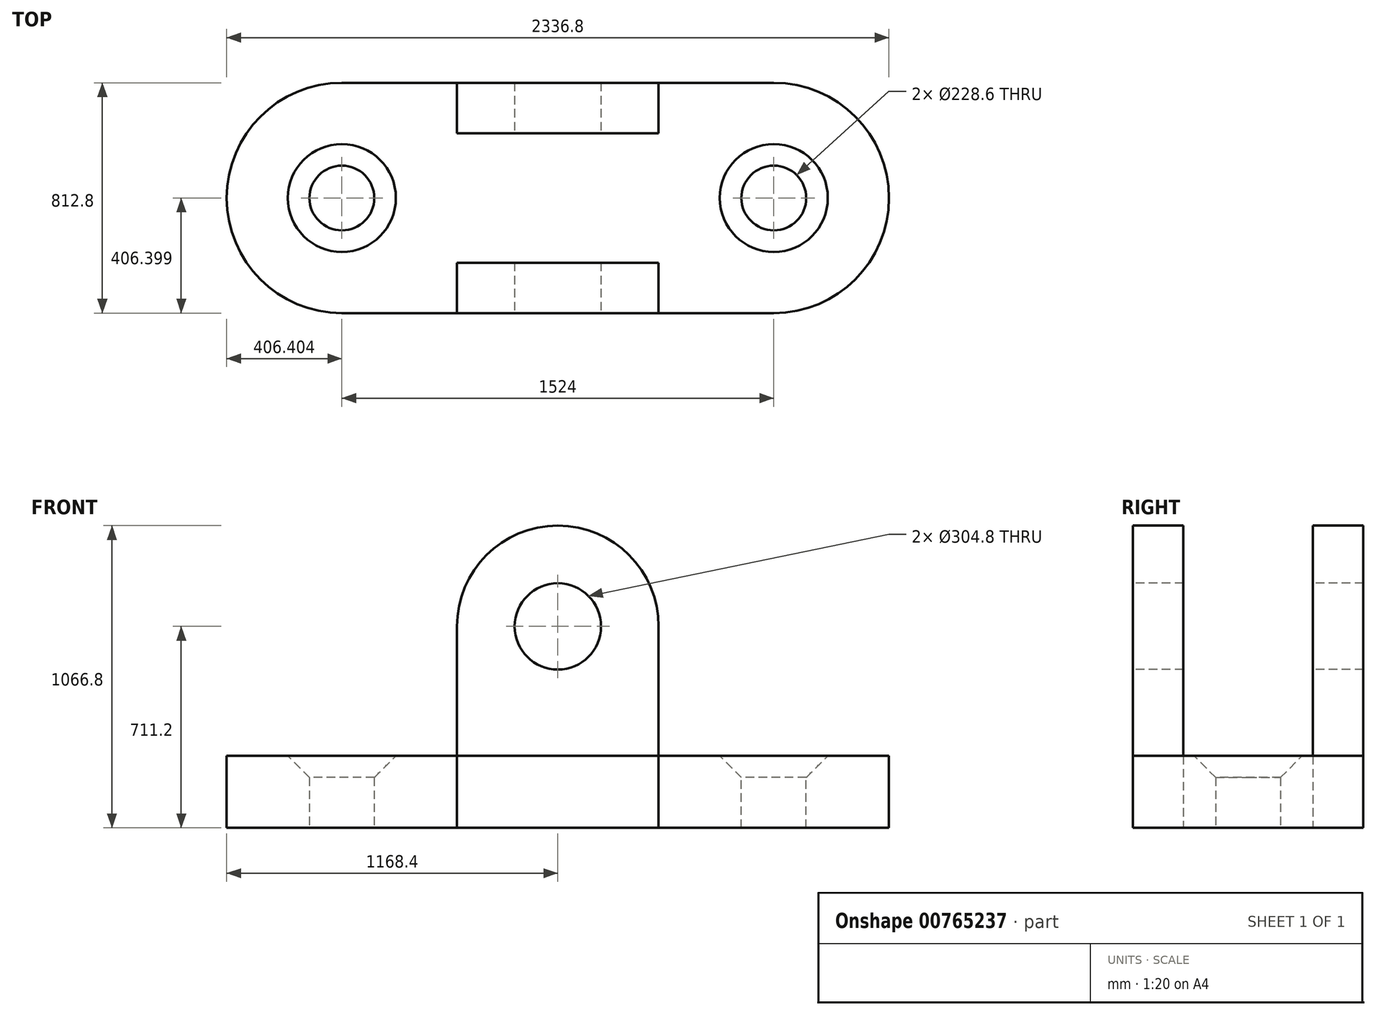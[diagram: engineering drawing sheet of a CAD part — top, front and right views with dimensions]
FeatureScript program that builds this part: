
annotation { "Feature Type Name" : "Feature", "Feature Type Description" : "" }
export const myFeature = defineFeature(function(context is Context, id is Id, definition is map)
    precondition{}
    {
        {
            var Q0;
            Q0=qCreatedBy(makeId("Top.planeOp"),FACE);
            var sketch = newSketch(context, id + "F0", { "sketchPlane" : qUnion([Q0])});
            skLineSegment(sketch, "E0.top", {"start": v(-545.79, -124.18) * mm, "end": v(1791.01, -124.18) * mm});
            skLineSegment(sketch, "E0.left", {"start": v(-545.79, 688.62) * mm, "end": v(-545.79, -124.18) * mm});
            skLineSegment(sketch, "E0.right", {"start": v(1791.01, 688.62) * mm, "end": v(1791.01, -124.18) * mm});
            skLineSegment(sketch, "E1", {"start": v(-545.79, 688.62) * mm, "end": v(1791.01, 688.62) * mm});
            skLineSegment(sketch, "E2", {"start": v(-545.79, 688.62) * mm, "end": v(-545.79, 282.22) * mm});
            skLineSegment(sketch, "E3", {"start": v(-545.79, 282.22) * mm, "end": v(-139.39, 282.22) * mm});
            skCircle(sketch, "E4", {"center": v(-139.39, 282.22) * mm, "radius": 406.4 * mm});
            skLineSegment(sketch, "E5", {"start": v(-139.39, 282.22) * mm, "end": v(-253.69, 282.22) * mm});
            skLineSegment(sketch, "E6", {"start": v(-139.39, 282.22) * mm, "end": v(-342.59, 282.22) * mm});
            skCircle(sketch, "E7", {"center": v(-139.39, 282.22) * mm, "radius": 114.3 * mm});
            skLineSegment(sketch, "E8", {"start": v(1791.01, 688.62) * mm, "end": v(1791.01, 282.22) * mm});
            skLineSegment(sketch, "E9", {"start": v(1791.01, 282.22) * mm, "end": v(1384.61, 282.22) * mm});
            skLineSegment(sketch, "E10", {"start": v(1384.61, 282.22) * mm, "end": v(1498.91, 282.22) * mm});
            skLineSegment(sketch, "E11", {"start": v(1384.61, 282.22) * mm, "end": v(1587.81, 282.22) * mm});
            skCircle(sketch, "E12", {"center": v(1384.61, 282.22) * mm, "radius": 406.4 * mm});
            skLineSegment(sketch, "E13", {"start": v(-139.39, 282.22) * mm, "end": v(267.01, 282.22) * mm});
            skLineSegment(sketch, "E14", {"start": v(267.01, 282.22) * mm, "end": v(267.01, 688.62) * mm});
            skLineSegment(sketch, "E15", {"start": v(267.01, 282.22) * mm, "end": v(267.01, -124.18) * mm});
            skLineSegment(sketch, "E16", {"start": v(1384.61, 282.22) * mm, "end": v(978.21, 282.22) * mm});
            skLineSegment(sketch, "E17", {"start": v(978.21, 282.22) * mm, "end": v(978.21, 688.62) * mm});
            skLineSegment(sketch, "E18", {"start": v(978.21, 282.22) * mm, "end": v(978.21, -124.18) * mm});
            skLineSegment(sketch, "E19", {"start": v(267.01, -124.18) * mm, "end": v(267.01, 53.62) * mm});
            skLineSegment(sketch, "E20", {"start": v(978.21, -124.18) * mm, "end": v(978.21, 53.62) * mm});
            skLineSegment(sketch, "E21", {"start": v(267.01, 53.62) * mm, "end": v(978.21, 53.62) * mm});
            skLineSegment(sketch, "E22", {"start": v(267.01, 688.62) * mm, "end": v(267.01, 510.82) * mm});
            skLineSegment(sketch, "E23", {"start": v(978.21, 688.62) * mm, "end": v(978.21, 510.82) * mm});
            skLineSegment(sketch, "E24", {"start": v(267.01, 510.82) * mm, "end": v(978.21, 510.82) * mm});
            skSolve(sketch);
        }
        {
            var Q0;
            {var subQ5=sQuery(id+"F0.wireOp",EDGE,"E21");Q0=makeQuery(id+"F0.imprint","IMPRINT",FACE,{"disambiguationData":[TD([[makeQuery(id+"F0.imprint","IMPRINT",EDGE,{"derivedFrom":subQ5}),-1.0]])]});}
            var Q1;
            {var subQ5=sQuery(id+"F0.wireOp",EDGE,"E24");Q1=makeQuery(id+"F0.imprint","IMPRINT",FACE,{"disambiguationData":[TD([[makeQuery(id+"F0.imprint","IMPRINT",EDGE,{"derivedFrom":subQ5}),1.0]])]});}
            extrude(context, id + "F1", {"entities" : qUnion([Q0, Q1]), "depth" : 711.2 * mm, "offsetDistance" : 25.4 * mm});
        }
        {
            var Q0;
            {var subQ0=sQuery(id+"F0.wireOp",EDGE,"E0.left");var subQ1=sQuery(id+"F0.wireOp",EDGE,"E0.top");var subQ2=makeQuery(id+"F0.imprint","INTERSECT",VERTEX,{"derivedFrom":[subQ1,subQ0]});Q0=makeQuery(id+"F0.imprint","IMPRINT",FACE,{"disambiguationData":[TD([[makeQuery(id+"F0.imprint","IMPRINT",EDGE,{"disambiguationData":[TD([[subQ2,-1.0]])],"derivedFrom":subQ1}),1.0]])]});}
            var Q1;
            {var subQ0=sQuery(id+"F0.wireOp",EDGE,"E12");var subQ1=sQuery(id+"F0.wireOp",EDGE,"E0.top");var subQ2=makeQuery(id+"F0.imprint","INTERSECT",VERTEX,{"derivedFrom":[subQ1,subQ0]});Q1=makeQuery(id+"F0.imprint","IMPRINT",FACE,{"disambiguationData":[TD([[makeQuery(id+"F0.imprint","IMPRINT",EDGE,{"disambiguationData":[TD([[subQ2,-1.0]])],"derivedFrom":subQ1}),1.0]])]});}
            var Q2;
            {var subQ0=sQuery(id+"F0.wireOp",EDGE,"E1");var subQ1=sQuery(id+"F0.wireOp",EDGE,"E0.left");var subQ2=makeQuery(id+"F0.imprint","INTERSECT",VERTEX,{"derivedFrom":[subQ1,subQ0]});Q2=makeQuery(id+"F0.imprint","IMPRINT",FACE,{"disambiguationData":[TD([[makeQuery(id+"F0.imprint","IMPRINT",EDGE,{"disambiguationData":[TD([[subQ2,-1.0]])],"derivedFrom":subQ0}),-1.0]])]});}
            var Q3;
            {var subQ1=sQuery(id+"F0.wireOp",EDGE,"E0.right");var subQ3=sQuery(id+"F0.wireOp",EDGE,"E1");var subQ4=makeQuery(id+"F0.imprint","INTERSECT",VERTEX,{"derivedFrom":[subQ1,subQ3]});Q3=makeQuery(id+"F0.imprint","IMPRINT",FACE,{"disambiguationData":[TD([[makeQuery(id+"F0.imprint","IMPRINT",EDGE,{"disambiguationData":[TD([[subQ4,1.0]])],"derivedFrom":subQ3}),-1.0]])]});}
            var Q4;
            {var subQ5=sQuery(id+"F0.wireOp",EDGE,"E21");Q4=makeQuery(id+"F0.imprint","IMPRINT",FACE,{"disambiguationData":[TD([[makeQuery(id+"F0.imprint","IMPRINT",EDGE,{"derivedFrom":subQ5}),-1.0]])]});}
            var Q5;
            {var subQ0=sQuery(id+"F0.wireOp",EDGE,"E12");var subQ1=sQuery(id+"F0.wireOp",EDGE,"E0.top");var subQ2=makeQuery(id+"F0.imprint","INTERSECT",VERTEX,{"derivedFrom":[subQ1,subQ0]});Q5=makeQuery(id+"F0.imprint","IMPRINT",FACE,{"disambiguationData":[TD([[makeQuery(id+"F0.imprint","IMPRINT",EDGE,{"disambiguationData":[TD([[subQ2,1.0]])],"derivedFrom":subQ1}),1.0]])]});}
            var Q6;
            {var subQ0=sQuery(id+"F0.wireOp",EDGE,"E14");var subQ1=sQuery(id+"F0.wireOp",EDGE,"E1");var subQ2=makeQuery(id+"F0.imprint","INTERSECT",VERTEX,{"derivedFrom":[subQ1,subQ0]});Q6=makeQuery(id+"F0.imprint","IMPRINT",FACE,{"disambiguationData":[TD([[makeQuery(id+"F0.imprint","IMPRINT",EDGE,{"disambiguationData":[TD([[subQ2,1.0]])],"derivedFrom":subQ1}),-1.0]])]});}
            var Q7;
            {var subQ5=sQuery(id+"F0.wireOp",EDGE,"E24");Q7=makeQuery(id+"F0.imprint","IMPRINT",FACE,{"disambiguationData":[TD([[makeQuery(id+"F0.imprint","IMPRINT",EDGE,{"derivedFrom":subQ5}),1.0]])]});}
            var Q8;
            {var subQ0=sQuery(id+"F0.wireOp",EDGE,"E17");var subQ1=sQuery(id+"F0.wireOp",EDGE,"E1");var subQ2=makeQuery(id+"F0.imprint","INTERSECT",VERTEX,{"derivedFrom":[subQ1,subQ0]});Q8=makeQuery(id+"F0.imprint","IMPRINT",FACE,{"disambiguationData":[TD([[makeQuery(id+"F0.imprint","IMPRINT",EDGE,{"disambiguationData":[TD([[subQ2,-1.0]])],"derivedFrom":subQ1}),-1.0]])]});}
            var Q9;
            {var subQ1=sQuery(id+"F0.wireOp",EDGE,"E3");var subQ8=makeQuery(id+"F0.imprint","IMPRINT",VERTEX,{"derivedFrom":subQ1});Q9=makeQuery(id+"F0.imprint","IMPRINT",FACE,{"disambiguationData":[TD([[makeQuery(id+"F0.imprint","IMPRINT",EDGE,{"disambiguationData":[TD([[subQ8,-1.0]])],"derivedFrom":subQ1}),1.0]])]});}
            var Q10;
            {var subQ5=sQuery(id+"F0.wireOp",EDGE,"E3");var subQ7=makeQuery(id+"F0.imprint","IMPRINT",VERTEX,{"derivedFrom":subQ5});Q10=makeQuery(id+"F0.imprint","IMPRINT",FACE,{"disambiguationData":[TD([[makeQuery(id+"F0.imprint","IMPRINT",EDGE,{"disambiguationData":[TD([[subQ7,-1.0]])],"derivedFrom":subQ5}),-1.0]])]});}
            var Q11;
            {var subQ6=sQuery(id+"F0.wireOp",EDGE,"E16");Q11=makeQuery(id+"F0.imprint","IMPRINT",FACE,{"disambiguationData":[TD([[makeQuery(id+"F0.imprint","IMPRINT",EDGE,{"derivedFrom":subQ6}),-1.0]])]});}
            var Q12;
            {var subQ3=sQuery(id+"F0.wireOp",EDGE,"E16");Q12=makeQuery(id+"F0.imprint","IMPRINT",FACE,{"disambiguationData":[TD([[makeQuery(id+"F0.imprint","IMPRINT",EDGE,{"derivedFrom":subQ3}),1.0]])]});}
            var Q13;
            {var subQ0=sQuery(id+"F0.wireOp",EDGE,"E15");var subQ1=sQuery(id+"F0.wireOp",EDGE,"E0.top");var subQ2=makeQuery(id+"F0.imprint","INTERSECT",VERTEX,{"derivedFrom":[subQ1,subQ0]});Q13=makeQuery(id+"F0.imprint","IMPRINT",FACE,{"disambiguationData":[TD([[makeQuery(id+"F0.imprint","IMPRINT",EDGE,{"disambiguationData":[TD([[subQ2,1.0]])],"derivedFrom":subQ1}),1.0]])]});}
            var Q14;
            {var subQ3=sQuery(id+"F0.wireOp",EDGE,"E21");Q14=makeQuery(id+"F0.imprint","IMPRINT",FACE,{"disambiguationData":[TD([[makeQuery(id+"F0.imprint","IMPRINT",EDGE,{"derivedFrom":subQ3}),1.0]])]});}
            extrude(context, id + "F2", {"entities" : qUnion([Q0, Q1, Q2, Q3, Q4, Q5, Q6, Q7, Q8, Q9, Q10, Q11, Q12, Q13, Q14]), "depth" : 254 * mm, "offsetDistance" : 25.4 * mm});
        }
        {
            var Q0;
            Q0=makeQuery(id+"F1.opExtrude","SWEPT_FACE",FACE,{"disambiguationData":[OSD([sQuery(id+"F0.wireOp",EDGE,"E0.top")])]});
            var sketch = newSketch(context, id + "F3", { "sketchPlane" : qUnion([Q0])});
            skLineSegment(sketch, "E25", {"start": v(267.01, 0) * mm, "end": v(267.01, 254) * mm});
            skCircle(sketch, "E26", {"center": v(622.61, 711.2) * mm, "radius": 355.6 * mm});
            skSolve(sketch);
        }
        {
            var Q0;
            {var subQ1=sQuery(id+"F0.wireOp",EDGE,"E0.top");var subQ2=makeQuery(id+"F1.opExtrude","CAP_EDGE",EDGE,{"disambiguationData":[OSD([subQ1])],"isStart":false});Q0=makeQuery(id+"F3.imprint","IMPRINT",FACE,{"disambiguationData":[TD([[makeQuery(id+"F3.imprint","IMPRINT",EDGE,{"derivedFrom":subQ2}),1.0]])]});}
            var Q1;
            {var subQ1=sQuery(id+"F0.wireOp",EDGE,"E0.top");var subQ2=makeQuery(id+"F1.opExtrude","CAP_EDGE",EDGE,{"disambiguationData":[OSD([subQ1])],"isStart":false});Q1=makeQuery(id+"F3.imprint","IMPRINT",FACE,{"disambiguationData":[TD([[makeQuery(id+"F3.imprint","IMPRINT",EDGE,{"derivedFrom":subQ2}),-1.0]])]});}
            extrude(context, id + "F4", {"entities" : qUnion([Q0, Q1]), "operationType" : NewBodyOperationType.ADD, "depth" : 0 * mm, "offsetDistance" : 25.4 * mm, "hasSecondDirection" : true, "secondDirectionOppositeDirection" : true, "secondDirectionDepth" : 177.8 * mm});
        }
        {
            var Q0;
            Q0=makeQuery(id+"F1.opExtrude","SWEPT_FACE",FACE,{"disambiguationData":[OSD([sQuery(id+"F0.wireOp",EDGE,"E1")])]});
            var sketch = newSketch(context, id + "F5", { "sketchPlane" : qUnion([Q0])});
            skCircle(sketch, "E27", {"center": v(-622.61, 711.2) * mm, "radius": 355.6 * mm});
            skSolve(sketch);
        }
        {
            var Q0;
            {var subQ1=sQuery(id+"F0.wireOp",EDGE,"E1");var subQ2=makeQuery(id+"F1.opExtrude","CAP_EDGE",EDGE,{"disambiguationData":[OSD([subQ1])],"isStart":false});Q0=makeQuery(id+"F5.imprint","IMPRINT",FACE,{"disambiguationData":[TD([[makeQuery(id+"F5.imprint","IMPRINT",EDGE,{"derivedFrom":subQ2}),-1.0]])]});}
            extrude(context, id + "F6", {"entities" : qUnion([Q0]), "operationType" : NewBodyOperationType.ADD, "depth" : 0 * mm, "offsetDistance" : 25.4 * mm, "hasSecondDirection" : true, "secondDirectionOppositeDirection" : true, "secondDirectionDepth" : 177.8 * mm});
        }
        {
            var Q0;
            Q0=makeQuery(id+"F2.opExtrude","SWEPT_EDGE",EDGE,{"disambiguationData":[OSD([sQuery(id+"F0.wireOp",EDGE,"E0.left"),sQuery(id+"F0.wireOp",EDGE,"E1")])]});
            fillet(context, id + "F7", {"entities" : qUnion([Q0]), "radius" : 406.4 * mm, "tangentPropagation" : true, "allowEdgeOverflow" : false});
        }
        {
            var Q0;
            Q0=makeQuery(id+"F2.opExtrude","SWEPT_EDGE",EDGE,{"disambiguationData":[OSD([sQuery(id+"F0.wireOp",EDGE,"E0.top"),sQuery(id+"F0.wireOp",EDGE,"E0.left")])]});
            fillet(context, id + "F8", {"entities" : qUnion([Q0]), "radius" : 406.4 * mm, "tangentPropagation" : true, "allowEdgeOverflow" : false});
        }
        {
            var Q0;
            Q0=makeQuery(id+"F2.opExtrude","SWEPT_EDGE",EDGE,{"disambiguationData":[OSD([sQuery(id+"F0.wireOp",EDGE,"E0.top"),sQuery(id+"F0.wireOp",EDGE,"E0.right")])]});
            fillet(context, id + "F9", {"entities" : qUnion([Q0]), "radius" : 406.4 * mm, "tangentPropagation" : true, "allowEdgeOverflow" : false});
        }
        {
            var Q0;
            Q0=makeQuery(id+"F2.opExtrude","SWEPT_EDGE",EDGE,{"disambiguationData":[OSD([sQuery(id+"F0.wireOp",EDGE,"E0.right"),sQuery(id+"F0.wireOp",EDGE,"E1")])]});
            fillet(context, id + "F10", {"entities" : qUnion([Q0]), "radius" : 406.4 * mm, "tangentPropagation" : true, "allowEdgeOverflow" : false});
        }
        {
            var Q0;
            Q0=sQuery(id+"F3.wireOp",VERTEX,"E26.center");
            var Q1;
            Q1=makeQuery(id+"F1.opExtrude","SWEPT_BODY",BODY,{"disambiguationData":[OSD([sQuery(id+"F0.wireOp",EDGE,"E0.top"),sQuery(id+"F0.wireOp",EDGE,"E15"),sQuery(id+"F0.wireOp",EDGE,"E18"),sQuery(id+"F0.wireOp",EDGE,"E21")])]});
            var Q2;
            Q2=makeQuery(id+"F1.opExtrude","SWEPT_BODY",BODY,{"disambiguationData":[OSD([sQuery(id+"F0.wireOp",EDGE,"E1"),sQuery(id+"F0.wireOp",EDGE,"E14"),sQuery(id+"F0.wireOp",EDGE,"E17"),sQuery(id+"F0.wireOp",EDGE,"E24")])]});
            hole(context, id + "F11", {"style" : HoleStyle.SIMPLE, "endStyle" : HoleEndStyle.THROUGH, "holeDiameter" : 304.8 * mm, "majorDiameter" : 6.35 * mm, "isTappedThrough" : true, "tappedDepth" : 12.7 * mm, "tapClearance" : 3, "locations" : qUnion([Q0]), "scope" : qUnion([Q1, Q2])});
        }
        {
            var Q0;
            Q0=makeQuery(id+"F2.opExtrude","CAP_FACE",FACE,{"disambiguationData":[OSD([sQuery(id+"F0.wireOp",EDGE,"E0.top"),sQuery(id+"F0.wireOp",EDGE,"E0.left"),sQuery(id+"F0.wireOp",EDGE,"E0.right"),sQuery(id+"F0.wireOp",EDGE,"E1"),sQuery(id+"F0.wireOp",EDGE,"E7")])],"isStart":false});
            var sketch = newSketch(context, id + "F12", { "sketchPlane" : qUnion([Q0])});
            skLineSegment(sketch, "E28", {"start": v(-139.39, 282.22) * mm, "end": v(-139.39, 688.62) * mm});
            skLineSegment(sketch, "E29", {"start": v(-139.39, 688.62) * mm, "end": v(-139.39, 282.22) * mm});
            skLineSegment(sketch, "E30", {"start": v(-139.39, -124.18) * mm, "end": v(-139.39, 282.22) * mm});
            skLineSegment(sketch, "E31", {"start": v(1384.61, 282.22) * mm, "end": v(1384.61, 688.62) * mm});
            skLineSegment(sketch, "E32", {"start": v(1384.61, 688.62) * mm, "end": v(1384.61, -124.18) * mm});
            skSolve(sketch);
        }
        {
            var Q0;
            Q0=sQuery(id+"F12.wireOp",VERTEX,"E28.start");
            var Q1;
            Q1=sQuery(id+"F12.wireOp",VERTEX,"E31.start");
            var Q2;
            Q2=makeQuery(id+"F2.opExtrude","SWEPT_BODY",BODY,{"disambiguationData":[OSD([sQuery(id+"F0.wireOp",EDGE,"E0.top"),sQuery(id+"F0.wireOp",EDGE,"E0.left"),sQuery(id+"F0.wireOp",EDGE,"E0.right"),sQuery(id+"F0.wireOp",EDGE,"E1"),sQuery(id+"F0.wireOp",EDGE,"E7")])]});
            hole(context, id + "F13", {"style" : HoleStyle.C_SINK, "endStyle" : HoleEndStyle.THROUGH, "holeDiameter" : 228.6 * mm, "cSinkDiameter" : 381 * mm, "cSinkAngle" : 90 * degree, "majorDiameter" : 6.35 * mm, "isTappedThrough" : true, "tappedDepth" : 12.7 * mm, "tapClearance" : 3, "startFromSketch" : true, "locations" : qUnion([Q0, Q1]), "scope" : qUnion([Q2])});
        }
    });
